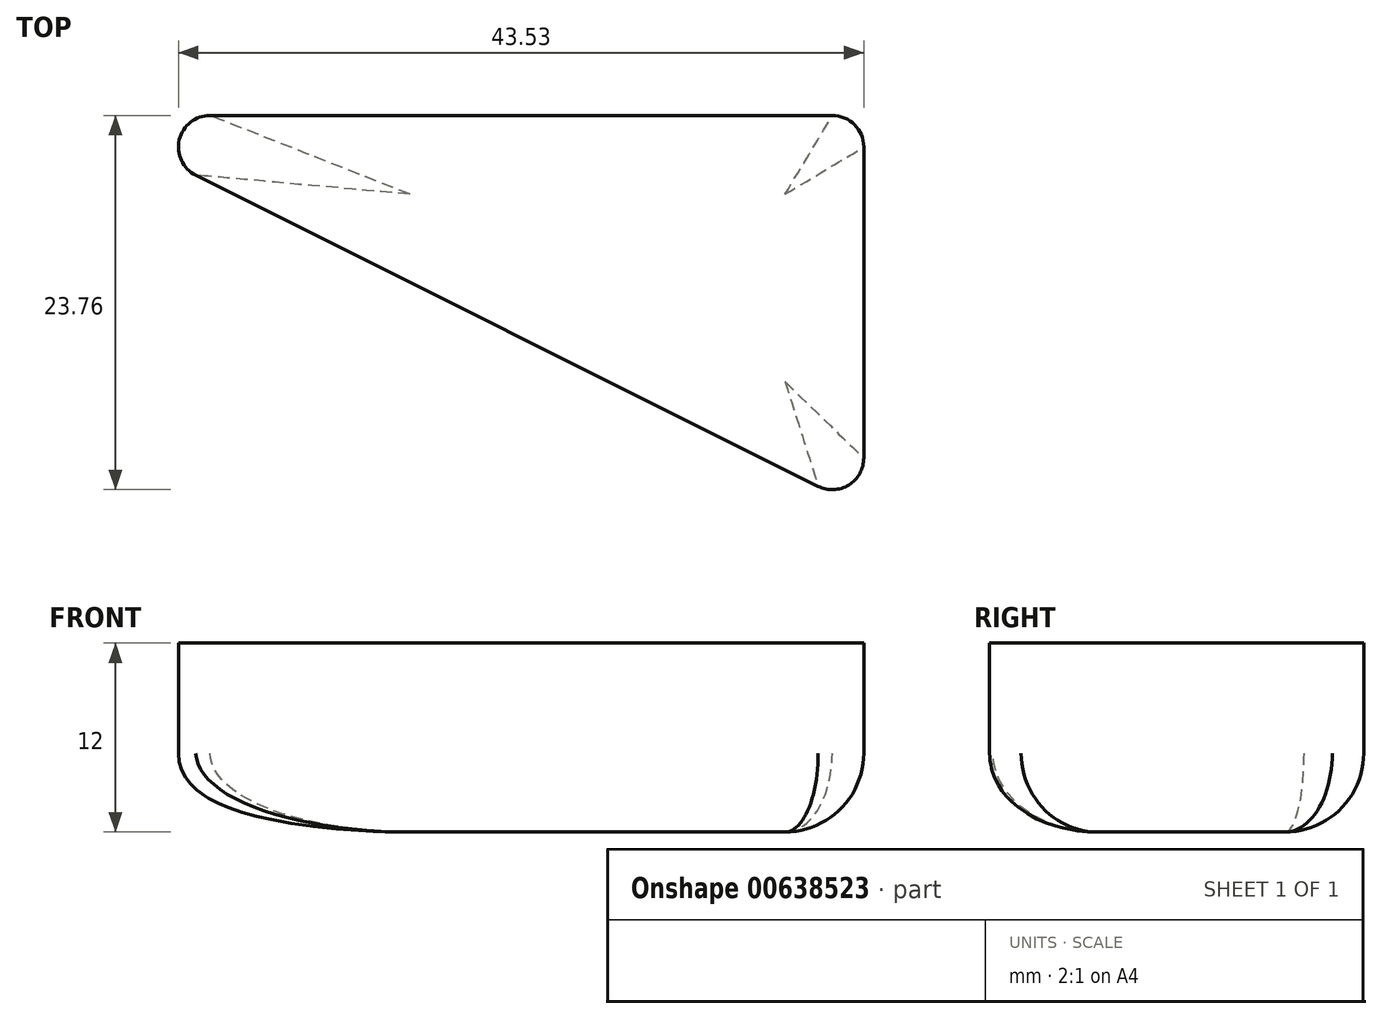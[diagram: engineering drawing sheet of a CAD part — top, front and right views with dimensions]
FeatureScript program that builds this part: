
annotation { "Feature Type Name" : "Feature", "Feature Type Description" : "" }
export const myFeature = defineFeature(function(context is Context, id is Id, definition is map)
    precondition{}
    {
        {
            var Q0;
            Q0=qCreatedBy(makeId("Top.planeOp"),FACE);
            var sketch = newSketch(context, id + "F0", { "sketchPlane" : qUnion([Q0])});
            skPoint(sketch, "E0", {"position": v(0, 0) * mm});
            skPoint(sketch, "E1", {"position": v(0, -40) * mm});
            skPoint(sketch, "E2", {"position": v(40, 0) * mm});
            skArc(sketch, "E3.MirrorCS", {"start": v(-52.42, -13.79) * mm, "mid": v(-53.47, -11.54) * mm, "end": v(-51.53, -10) * mm});
            skArc(sketch, "E4.MirrorCS", {"start": v(-10, -31.76) * mm, "mid": v(-10.95, -33.47) * mm, "end": v(-12.9, -33.55) * mm});
            skArc(sketch, "E5.MirrorCS", {"start": v(-12, -10) * mm, "mid": v(-10.59, -10.59) * mm, "end": v(-10, -12) * mm});
            skPoint(sketch, "E6.MirrorP", {"position": v(-10, -10) * mm});
            skPoint(sketch, "E7.MirrorP", {"position": v(-80, 0) * mm});
            skPoint(sketch, "E8.MirrorP", {"position": v(-10, -35) * mm});
            skPoint(sketch, "E9.MirrorP", {"position": v(-40, 0) * mm});
            skLineSegment(sketch, "E10.MirrorCS", {"start": v(-10, -12) * mm, "end": v(-10, -31.76) * mm});
            skLineSegment(sketch, "E11.MirrorCS", {"start": v(-12, -10) * mm, "end": v(-51.53, -10) * mm});
            skLineSegment(sketch, "E12.MirrorCS", {"start": v(-52.42, -13.79) * mm, "end": v(-12.9, -33.55) * mm});
            skLineSegment(sketch, "E13.MirrorCS", {"start": v(-84.47, -8.94) * mm, "end": v(-4.47, -48.94) * mm});
            skLineSegment(sketch, "E14.MirrorCS", {"start": v(0, 10) * mm, "end": v(-80, 10) * mm});
            skArc(sketch, "E15.MirrorCS", {"start": v(10, -40) * mm, "mid": v(5.26, -48.5) * mm, "end": v(-4.47, -48.94) * mm});
            skArc(sketch, "E16.MirrorCS", {"start": v(-84.47, -8.94) * mm, "mid": v(-89.73, 2.3) * mm, "end": v(-80, 10) * mm});
            skArc(sketch, "E17.MirrorCS", {"start": v(0, 10) * mm, "mid": v(7.07, 7.07) * mm, "end": v(10, 0) * mm});
            skPoint(sketch, "E18.MirrorP", {"position": v(-60, -10) * mm});
            skLineSegment(sketch, "E19", {"start": v(10, 0) * mm, "end": v(10, -40) * mm});
            skPoint(sketch, "E20", {"position": v(0, -15) * mm});
            skSolve(sketch);
        }
        {
            var Q0;
            Q0=makeQuery(id+"F0.imprint","IMPRINT",FACE,{"disambiguationData":[TD([[makeQuery(id+"F0.imprint","IMPRINT",EDGE,{"derivedFrom":sQuery(id+"F0.wireOp",EDGE,"E3.MirrorCS")}),1.0]])]});
            extrude(context, id + "F1", {"entities" : qUnion([Q0]), "depth" : 12 * mm, "offsetDistance" : 25 * mm});
        }
        {
            var Q0;
            Q0=sQuery(id+"F0.wireOp",VERTEX,"E1");
            var Q1;
            Q1=sQuery(id+"F0.wireOp",VERTEX,"E9.MirrorP");
            var Q2;
            Q2=sQuery(id+"F0.wireOp",VERTEX,"E7.MirrorP");
            var Q3;
            Q3=sQuery(id+"F0.wireOp",VERTEX,"E20");
            var Q4;
            Q4=makeQuery(id+"F1.opExtrude","SWEPT_BODY",BODY,{"disambiguationData":[OSD([sQuery(id+"F0.wireOp",EDGE,"9XillGGi-X9Vl-tvCv-TnwF-3YY5MHNxSCeT"),sQuery(id+"F0.wireOp",EDGE,"NQ2yS7kT-hUOL-mdMV-tFRt-xZ6I2ecozLxp"),sQuery(id+"F0.wireOp",EDGE,"oTe80ukg-N24N-KCaY-E6PN-eS6dcYNLtXK0"),sQuery(id+"F0.wireOp",EDGE,"zOzAKUDD-R7aN-ZVnt-EghM-WRPQ8uhMQBrV"),sQuery(id+"F0.wireOp",EDGE,"cKX9bCXw-r3Hm-V8C6-tYqE-yRRbsqveWvlH"),sQuery(id+"F0.wireOp",EDGE,"K5019dLs-C7ti-J8hI-PWTG-TZ359QAl1vYJ"),sQuery(id+"F0.wireOp",EDGE,"8724d30a-445c-4b4a-b53a-b6f5be8d11d7.0"),sQuery(id+"F0.wireOp",EDGE,"352ad51d-7c13-4f12-8233-80c19cddfbec.0"),sQuery(id+"F0.wireOp",EDGE,"6e1ed7d2-2d2b-43c5-90e5-1fcae292d19a.0"),sQuery(id+"F0.wireOp",EDGE,"07220ac1-49d3-4d03-a8ad-f24c4112e699.filletArc"),sQuery(id+"F0.wireOp",EDGE,"b9f0f69f-3575-4922-bcc7-b2b8f647fde8.filletArc"),sQuery(id+"F0.wireOp",EDGE,"2f54f10e-a587-4344-b570-e26064604c3e.filletArc")])]});
            var Q5;
            Q5=makeQuery(id+"F1.opExtrude","SWEPT_BODY",BODY,{"disambiguationData":[OSD([sQuery(id+"F0.wireOp",EDGE,"E3.MirrorCS"),sQuery(id+"F0.wireOp",EDGE,"E4.MirrorCS"),sQuery(id+"F0.wireOp",EDGE,"E5.MirrorCS"),sQuery(id+"F0.wireOp",EDGE,"E10.MirrorCS"),sQuery(id+"F0.wireOp",EDGE,"E11.MirrorCS"),sQuery(id+"F0.wireOp",EDGE,"E12.MirrorCS"),sQuery(id+"F0.wireOp",EDGE,"E15.MirrorCS"),sQuery(id+"F0.wireOp",EDGE,"E17.MirrorCS"),sQuery(id+"F0.wireOp",EDGE,"E16.MirrorCS"),sQuery(id+"F0.wireOp",EDGE,"E14.MirrorCS"),sQuery(id+"F0.wireOp",EDGE,"E13.MirrorCS"),sQuery(id+"F0.wireOp",EDGE,"E19")])]});
            hole(context, id + "F2", {"style" : HoleStyle.C_BORE, "endStyle" : HoleEndStyle.THROUGH, "oppositeDirection" : true, "standardTappedOrClearance" : lookupTablePath({ "standard" : "ISO", "fit" : "Normal", "size" : "M5", "type" : "Clearance" }), "standardBlindInLast" : lookupTablePath({ "fit" : "Standard", "standard" : "ISO", "size" : "M5", "type" : "Clearance" }), "holeDiameter" : 5.5 * mm, "cBoreDiameter" : 9.75 * mm, "cBoreDepth" : 5 * mm, "majorDiameter" : 5 * mm, "isTappedThrough" : true, "tappedDepth" : 12 * mm, "tapClearance" : 3, "locations" : qUnion([Q0, Q1, Q2, Q3]), "scope" : qUnion([Q4, Q5])});
        }
        {
            var Q0;
            Q0=makeQuery(id+"F1.opExtrude","CAP_EDGE",EDGE,{"disambiguationData":[OSD([sQuery(id+"F0.wireOp",EDGE,"E14.MirrorCS")])],"isStart":true});
            var Q1;
            Q1=makeQuery(id+"F1.opExtrude","CAP_EDGE",EDGE,{"disambiguationData":[OSD([sQuery(id+"F0.wireOp",EDGE,"E11.MirrorCS")])],"isStart":true});
            fillet(context, id + "F3", {"entities" : qUnion([Q0, Q1]), "radius" : 5 * mm, "tangentPropagation" : true, "allowEdgeOverflow" : false});
        }
    });
